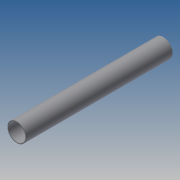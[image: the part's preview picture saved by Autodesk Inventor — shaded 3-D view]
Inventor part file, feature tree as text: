
AUTODESK INVENTOR PART (.ipt)
format: ipt  version: 2014 SP1 (Build 180222100, 222)  size: 122,880 bytes
history: native  units: in
note: dims shown in document units (in); Inventor stores cm internally (conversion verified against a paired STEP export)
features: extrude x1, sketch x1
ambient origin geometry x8: Origin, YZ Plane, XZ Plane, XY Plane, X Axis, Y Axis, Z Axis, Center Point
bodies: Solid1 (feature_tree)
feature tree (2):
  extrude  "Extrusion1"  Depth=33.4646in
  sketch  "Sketch1"  dims[d0=3.937in d1=0.175in d2=33.4646in d3=0.0in]
